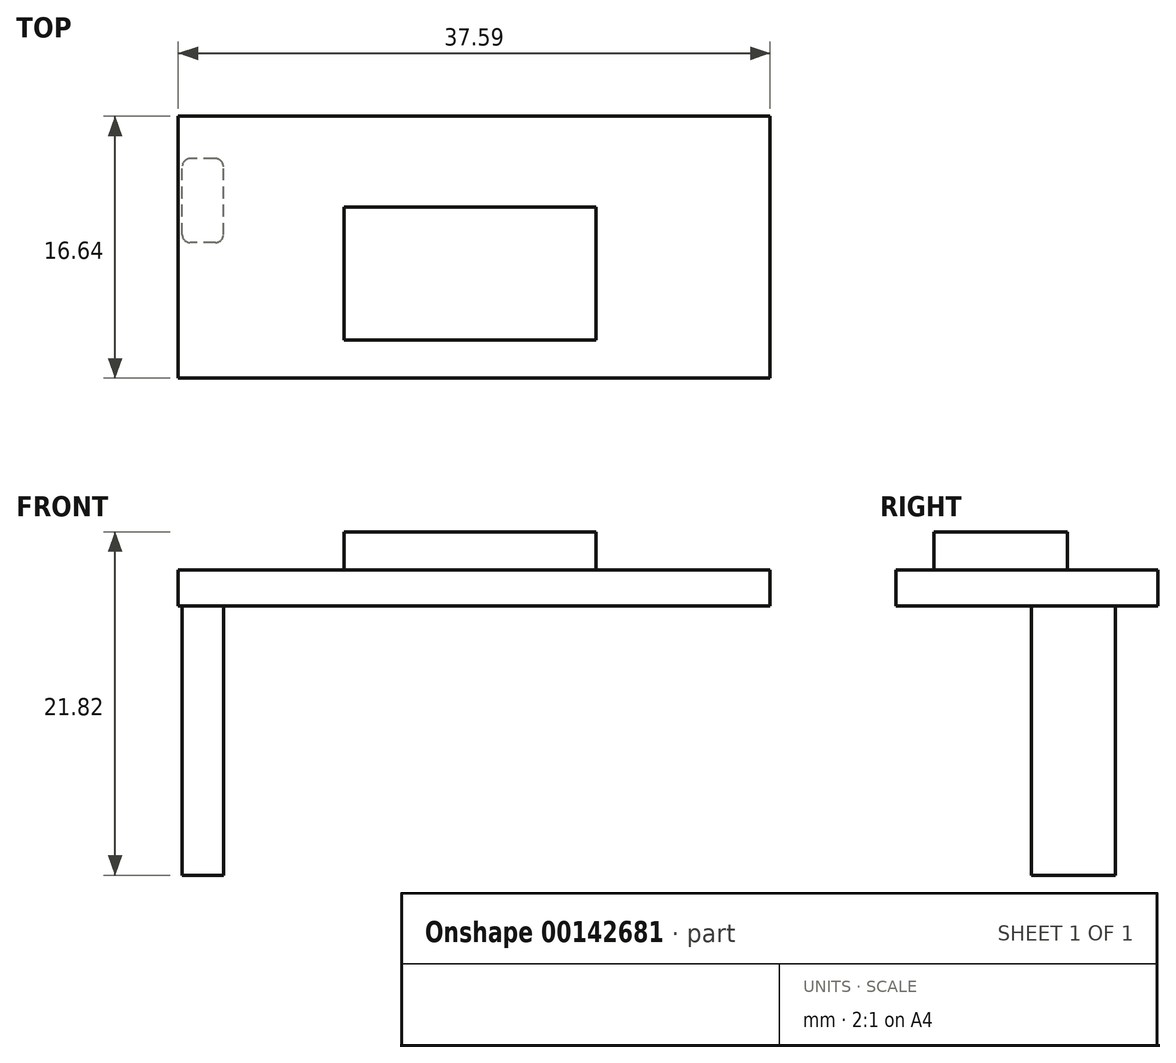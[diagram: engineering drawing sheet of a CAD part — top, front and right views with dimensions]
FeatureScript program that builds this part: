
annotation { "Feature Type Name" : "Feature", "Feature Type Description" : "" }
export const myFeature = defineFeature(function(context is Context, id is Id, definition is map)
    precondition{}
    {
        {
            var Q0;
            Q0=qCreatedBy(makeId("Top.planeOp"),FACE);
            var sketch = newSketch(context, id + "F0", { "sketchPlane" : qUnion([Q0])});
            skLineSegment(sketch, "E0.bottom", {"start": v(0, 0) * mm, "end": v(37.6, 0) * mm});
            skLineSegment(sketch, "E0.top", {"start": v(0, 16.64) * mm, "end": v(37.6, 16.64) * mm});
            skLineSegment(sketch, "E0.left", {"start": v(0, 0) * mm, "end": v(0, 16.64) * mm});
            skLineSegment(sketch, "E0.right", {"start": v(37.6, 0) * mm, "end": v(37.6, 16.64) * mm});
            skSolve(sketch);
        }
        {
            var Q0;
            Q0=makeQuery(id+"F0.imprint","IMPRINT",FACE,{"disambiguationData":[TD([[makeQuery(id+"F0.imprint","IMPRINT",EDGE,{"derivedFrom":sQuery(id+"F0.wireOp",EDGE,"E0.bottom")}),1.0]])]});
            extrude(context, id + "F1", {"entities" : qUnion([Q0]), "depth" : 2.3 * mm});
        }
        {
            var Q0;
            Q0=makeQuery(id+"F1.opExtrude","CAP_FACE",FACE,{"disambiguationData":[OSD([sQuery(id+"F0.wireOp",EDGE,"E0.bottom"),sQuery(id+"F0.wireOp",EDGE,"E0.top"),sQuery(id+"F0.wireOp",EDGE,"E0.left"),sQuery(id+"F0.wireOp",EDGE,"E0.right")])],"isStart":false});
            var sketch = newSketch(context, id + "F2", { "sketchPlane" : qUnion([Q0])});
            skLineSegment(sketch, "E1.bottom", {"start": v(10.54, 10.87) * mm, "end": v(26.54, 10.87) * mm});
            skLineSegment(sketch, "E1.top", {"start": v(10.54, 2.41) * mm, "end": v(26.54, 2.41) * mm});
            skLineSegment(sketch, "E1.left", {"start": v(10.54, 10.87) * mm, "end": v(10.54, 2.41) * mm});
            skLineSegment(sketch, "E1.right", {"start": v(26.54, 10.87) * mm, "end": v(26.54, 2.41) * mm});
            skSolve(sketch);
        }
        {
            var Q0;
            Q0=makeQuery(id+"F2.imprint","IMPRINT",FACE,{"disambiguationData":[TD([[makeQuery(id+"F2.imprint","IMPRINT",EDGE,{"derivedFrom":sQuery(id+"F2.wireOp",EDGE,"E1.bottom")}),-1.0]])]});
            extrude(context, id + "F3", {"entities" : qUnion([Q0]), "operationType" : NewBodyOperationType.ADD, "depth" : 2.41 * mm});
        }
        {
            var Q0;
            Q0=makeQuery(id+"F1.opExtrude","CAP_FACE",FACE,{"disambiguationData":[OSD([sQuery(id+"F0.wireOp",EDGE,"E0.bottom"),sQuery(id+"F0.wireOp",EDGE,"E0.top"),sQuery(id+"F0.wireOp",EDGE,"E0.left"),sQuery(id+"F0.wireOp",EDGE,"E0.right")])],"isStart":true});
            var sketch = newSketch(context, id + "F4", { "sketchPlane" : qUnion([Q0])});
            skLineSegment(sketch, "E2.bottom", {"start": v(2.87, -8.61) * mm, "end": v(0.25, -8.61) * mm});
            skLineSegment(sketch, "E2.top", {"start": v(2.87, -13.94) * mm, "end": v(0.25, -13.94) * mm});
            skLineSegment(sketch, "E2.left", {"start": v(2.87, -8.61) * mm, "end": v(2.87, -13.94) * mm});
            skLineSegment(sketch, "E2.right", {"start": v(0.25, -8.61) * mm, "end": v(0.25, -13.94) * mm});
            skSolve(sketch);
        }
        {
            var Q0;
            Q0 = qSketchRegion(id + "F4", true);
            extrude(context, id + "F5", {"entities" : qUnion([Q0]), "operationType" : NewBodyOperationType.ADD, "depth" : 17.12 * mm});
        }
        {
            var Q0;
            Q0=makeQuery(id+"F5.opExtrude","SWEPT_EDGE",EDGE,{"disambiguationData":[OSD([sQuery(id+"F4.wireOp",EDGE,"E2.top"),sQuery(id+"F4.wireOp",EDGE,"E2.left")])]});
            var Q1;
            Q1=makeQuery(id+"F5.opExtrude","SWEPT_EDGE",EDGE,{"disambiguationData":[OSD([sQuery(id+"F4.wireOp",EDGE,"E2.top"),sQuery(id+"F4.wireOp",EDGE,"E2.right")])]});
            var Q2;
            Q2=makeQuery(id+"F5.opExtrude","SWEPT_EDGE",EDGE,{"disambiguationData":[OSD([sQuery(id+"F4.wireOp",EDGE,"E2.bottom"),sQuery(id+"F4.wireOp",EDGE,"E2.left")])]});
            var Q3;
            Q3=makeQuery(id+"F5.opExtrude","SWEPT_EDGE",EDGE,{"disambiguationData":[OSD([sQuery(id+"F4.wireOp",EDGE,"E2.bottom"),sQuery(id+"F4.wireOp",EDGE,"E2.right")])]});
            fillet(context, id + "F6", {"entities" : qUnion([Q0, Q1, Q2, Q3]), "radius" : 0.5 * mm, "tangentPropagation" : true, "allowEdgeOverflow" : false});
        }
    });
